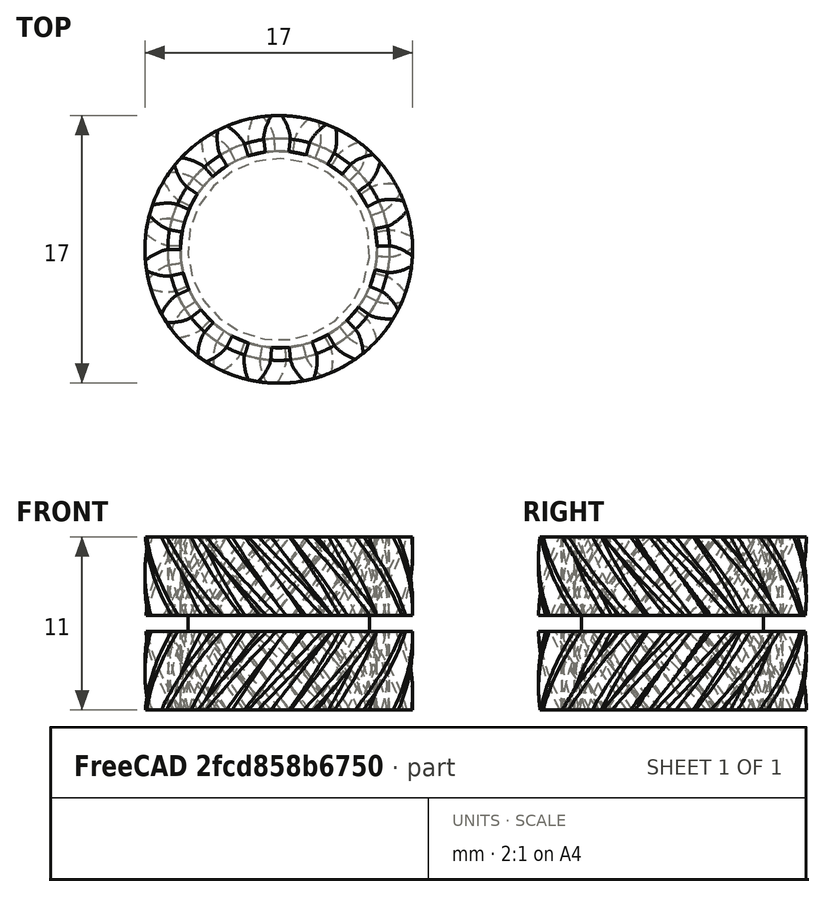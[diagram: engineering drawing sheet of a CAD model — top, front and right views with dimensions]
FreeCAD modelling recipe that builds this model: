
FCSTD DOCUMENT  (FreeCAD 0.21R33771 (Git))
Label: shevronnaja_shesternja
License: All rights reserved
LicenseURL: https://en.wikipedia.org/wiki/All_rights_reserved
objects: PartDesign::FeaturePython×2, Sketcher::SketchObject×1, PartDesign::Pad×1, PartDesign::Body×1
note: 6 computed .brp shape members not serialized (recipe doc carries the construction recipe); baked Part::Feature solids carry a one-line shape summary decoded from their .brp

FEATURE [PartDesign::FeaturePython] InvoluteGear  # WARN: FeaturePython — macro-defined, semantics opaque (R4)
  AttacherType = Attacher::AttachEngine3D
  Placement = pos=(0,0,0) rot=(0,0,1;-0.087266rad)
  angular_backlash = 0
  backlash = 0
  beta = 40
  clearance = 0.25
  da = 17
  df = 12.5
  double_helix = false
  dw = 15
  head = 0
  head_fillet = 0
  height = 5
  module = 1
  numpoints = 20
  pressure_angle = 20
  properties_from_tool = false
  reversed_backlash = false
  root_fillet = 0
  shift = 0
  simple = false
  teeth = 15
  transverse_pitch = 3.14159
  traverse_module = 1
  undercut = false
  version = 1.2.0
  expr: angular_backlash = backlash / dw * 360 ° / pi
FEATURE [Sketcher::SketchObject] Sketch
  FullyConstrained = false
  MapMode = 5
  Placement = pos=(6.63444e-05,3.38795e-05,5.00015) rot=(-8.4e-05,0.000149,-1;0.087266rad)
  Support = -> [InvoluteGear]
  sketch-geometry (1):
    g0: Circle CenterX=0 CenterY=0 CenterZ=0 NormalX=0 NormalY=0 NormalZ=1 AngleXU=0 Radius=5.77364
  constraints (1):
    c: Coincident(g0,g-1)
FEATURE [PartDesign::Pad] Pad
  BaseFeature = -> InvoluteGear
  Direction = (1.32685e-05,6.7757e-06,1)
  Length = 1
  Length2 = 10
  Placement = pos=(0,0,0) rot=(0,0,1;-0.087266rad)
  Profile = -> Sketch
  ReferenceAxis = -> Sketch [N_Axis]
  Type = 0
FEATURE [PartDesign::FeaturePython] InvoluteGear001  # WARN: FeaturePython — macro-defined, semantics opaque (R4)
  AttacherType = Attacher::AttachEngine3D
  BaseFeature = -> Pad
  Placement = pos=(0,0,6) rot=(0,0,1;0.05236rad)
  angular_backlash = 0
  backlash = 0
  beta = -40
  clearance = 0.25
  da = 17
  df = 12.5
  double_helix = false
  dw = 15
  head = 0
  head_fillet = 0
  height = 5
  module = 1
  numpoints = 20
  pressure_angle = 20
  properties_from_tool = false
  reversed_backlash = false
  root_fillet = 0
  shift = 0
  simple = false
  teeth = 15
  transverse_pitch = 3.14159
  traverse_module = 1
  undercut = false
  version = 1.2.0
  expr: angular_backlash = backlash / dw * 360 ° / pi
FEATURE [PartDesign::Body] Body
  Group = -> [InvoluteGear,Sketch,Pad,InvoluteGear001]
  Origin = -> Origin
  Tip = -> InvoluteGear001
